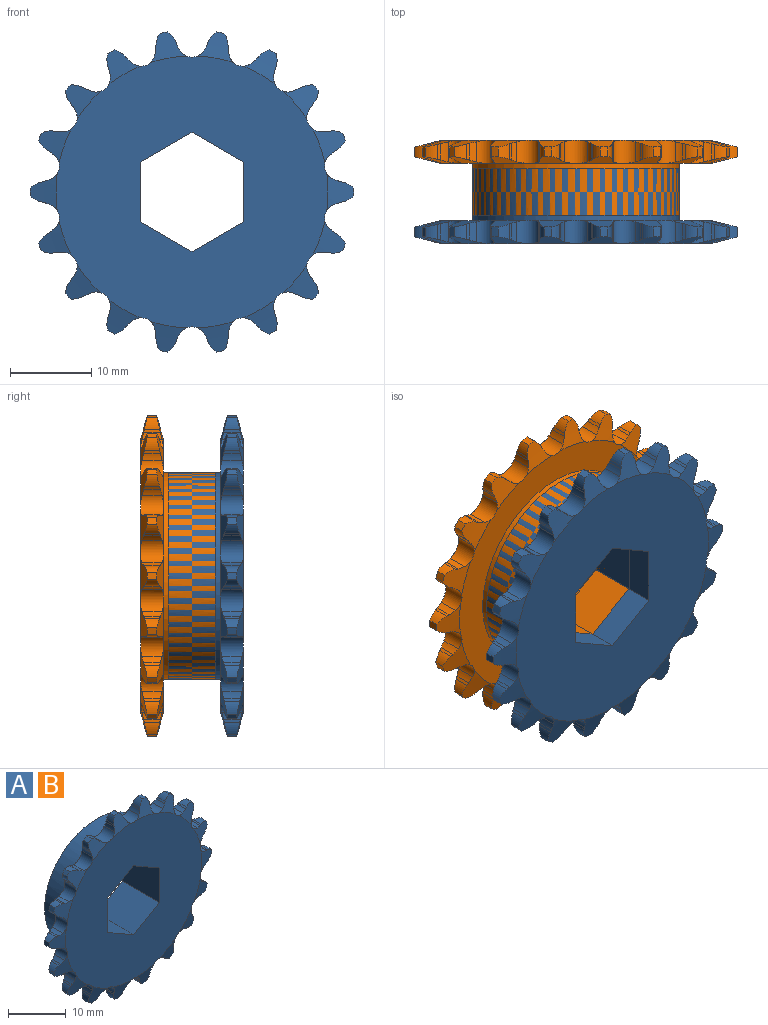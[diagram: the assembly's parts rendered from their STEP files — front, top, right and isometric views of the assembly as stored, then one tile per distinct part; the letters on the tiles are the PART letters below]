
ASSEMBLY  parts=2 mates=1
PART A: 190 faces, bbox 39.8x9.2x39.8 mm
  f0: cylinder r=12.7mm len=25.4mm, axis (0,-1,0), area 509.2mm2, adj f12,f183
  f1: cylinder r=1.74mm len=2.79mm, axis (0,1,0), area 9mm2, adj f12,f14,f16,f17,f20,f62,f170,f175
  f2: cylinder r=1.74mm len=2.79mm, axis (0,1,0), area 9mm2, adj f12,f17,f19,f20,f27,f62,f164,f169
  f3: cylinder r=1.74mm len=2.81mm, axis (0,1,0), area 9mm2, adj f11,f12,f19,f23,f27,f62,f158,f163
  f4: cylinder r=1.74mm len=2.81mm, axis (0,1,0), area 9mm2, adj f11,f12,f23,f25,f37,f62,f152,f157
  f5: cylinder r=1.74mm len=2.79mm, axis (0,1,0), area 9mm2, adj f12,f25,f28,f30,f37,f62,f146,f151
  f6: cylinder r=1.74mm len=2.79mm, axis (0,1,0), area 9mm2, adj f12,f28,f30,f31,f34,f62,f140,f145
  f7: cylinder r=2.72mm len=1.87mm, axis (0,1,0), area 2.4mm2, adj f40,f41,f42,f116
  f8: cylinder r=2.72mm len=1.87mm, axis (0,1,0), area 2.4mm2, adj f56,f57,f60,f80
  f9: cylinder r=19.91mm len=1.21mm, axis (0,1,0), area 1.1mm2, adj f10,f51,f95,f101
  f10: cone r=16.74mm half-angle=76deg, axis (0,1,0), area 8.4mm2, adj f9,f62,f95,f96,f97,f98,f99,f100
  f11: cone r=19.91mm half-angle=76deg, axis (0,-1,0), area 8.4mm2, adj f3,f4,f12,f24,f155,f156,f157,f158
  f12: plane 33.47x33.44mm, normal (0,1,0), area 370.7mm2, adj f0,f1,f2,f3,f4,f5,f6,f11
  f13: cone r=16.74mm half-angle=76deg, axis (0,1,0), area 8.4mm2, adj f61,f62,f65,f66,f67,f71,f179,f180
  f14: cone r=19.91mm half-angle=76deg, axis (0,-1,0), area 8.6mm2, adj f1,f12,f15,f173,f174,f175,f176,f177
  f15: cylinder r=19.91mm len=1.21mm, axis (0,1,0), area 1.1mm2, adj f14,f16,f173,f178
  f16: cone r=16.74mm half-angle=76deg, axis (0,1,0), area 8.6mm2, adj f1,f15,f62,f173,f174,f175,f176,f177
  f17: cone r=19.91mm half-angle=76deg, axis (0,-1,0), area 8.4mm2, adj f1,f2,f12,f18,f167,f168,f169,f170
  f18: cylinder r=19.91mm len=1.21mm, axis (0,1,0), area 1.1mm2, adj f17,f20,f167,f172
  f19: cone r=19.91mm half-angle=76deg, axis (0,-1,0), area 8.4mm2, adj f2,f3,f12,f21,f161,f162,f163,f164
  f20: cone r=16.74mm half-angle=76deg, axis (0,1,0), area 8.4mm2, adj f1,f2,f18,f62,f167,f168,f169,f170
  f21: cylinder r=19.91mm len=1.21mm, axis (0,1,0), area 1.1mm2, adj f19,f27,f161,f166
  f22: cone r=19.91mm half-angle=76deg, axis (0,-1,0), area 8.4mm2, adj f12,f61,f65,f66,f67,f71,f179,f180
  f23: cone r=16.74mm half-angle=76deg, axis (0,1,0), area 8.4mm2, adj f3,f4,f24,f62,f155,f156,f157,f158
  f24: cylinder r=19.91mm len=1.21mm, axis (0,1,0), area 1.1mm2, adj f11,f23,f155,f160
  f25: cone r=16.74mm half-angle=76deg, axis (0,1,0), area 8.4mm2, adj f4,f5,f26,f62,f149,f150,f151,f152
  f26: cylinder r=19.91mm len=1.21mm, axis (0,1,0), area 1.1mm2, adj f25,f37,f149,f154
  f27: cone r=16.74mm half-angle=76deg, axis (0,1,0), area 8.4mm2, adj f2,f3,f21,f62,f161,f162,f163,f164
  f28: cone r=19.91mm half-angle=76deg, axis (0,-1,0), area 8.4mm2, adj f5,f6,f12,f29,f143,f144,f145,f146
  f29: cylinder r=19.91mm len=1.21mm, axis (0,1,0), area 1.1mm2, adj f28,f30,f143,f148
  f30: cone r=16.74mm half-angle=76deg, axis (0,1,0), area 8.4mm2, adj f5,f6,f29,f62,f143,f144,f145,f146
  f31: cone r=19.91mm half-angle=76deg, axis (0,-1,0), area 8.6mm2, adj f6,f12,f32,f136,f137,f138,f139,f140
  f32: cylinder r=19.91mm len=1.21mm, axis (0,1,0), area 1.1mm2, adj f31,f34,f136,f142
  f33: cone r=19.91mm half-angle=76deg, axis (0,-1,0), area 8.4mm2, adj f12,f35,f129,f130,f131,f132,f133,f134
  f34: cone r=16.74mm half-angle=76deg, axis (0,1,0), area 8.6mm2, adj f6,f32,f62,f136,f137,f138,f139,f140
  f35: cylinder r=19.91mm len=1.21mm, axis (0,1,0), area 1.1mm2, adj f33,f39,f129,f135
  f36: cone r=16.74mm half-angle=76deg, axis (0,1,0), area 8.4mm2, adj f38,f62,f122,f123,f124,f125,f126,f127
  f37: cone r=19.91mm half-angle=76deg, axis (0,-1,0), area 8.4mm2, adj f4,f5,f12,f26,f149,f150,f151,f152
  f38: cylinder r=19.91mm len=1.21mm, axis (0,1,0), area 1.1mm2, adj f36,f48,f122,f128
  f39: cone r=16.74mm half-angle=76deg, axis (0,1,0), area 8.4mm2, adj f35,f62,f129,f130,f131,f132,f133,f134
  f40: cone r=19.91mm half-angle=76deg, axis (0,-1,0), area 8.5mm2, adj f7,f12,f41,f116,f117,f118,f119,f120
  f41: cylinder r=19.91mm len=1.21mm, axis (0,1,0), area 1.1mm2, adj f7,f40,f42,f121
  f42: cone r=16.74mm half-angle=76deg, axis (0,1,0), area 8.5mm2, adj f7,f41,f62,f116,f117,f118,f119,f120
  f43: cone r=19.91mm half-angle=76deg, axis (0,-1,0), area 8.4mm2, adj f12,f44,f109,f110,f111,f112,f113,f114
  f44: cylinder r=19.91mm len=1.21mm, axis (0,1,0), area 1.1mm2, adj f43,f46,f109,f115
  f45: cone r=19.91mm half-angle=76deg, axis (0,-1,0), area 8.4mm2, adj f12,f47,f102,f103,f104,f105,f106,f107
  f46: cone r=16.74mm half-angle=76deg, axis (0,1,0), area 8.4mm2, adj f44,f62,f109,f110,f111,f112,f113,f114
  f47: cylinder r=19.91mm len=1.21mm, axis (0,1,0), area 1.1mm2, adj f45,f52,f102,f108
  f48: cone r=19.91mm half-angle=76deg, axis (0,-1,0), area 8.4mm2, adj f12,f38,f122,f123,f124,f125,f126,f127
  f49: cone r=16.74mm half-angle=76deg, axis (0,1,0), area 8.4mm2, adj f50,f62,f88,f89,f90,f91,f92,f93
  f50: cylinder r=19.91mm len=1.21mm, axis (0,1,0), area 1.1mm2, adj f49,f63,f88,f94
  f51: cone r=19.91mm half-angle=76deg, axis (0,-1,0), area 8.4mm2, adj f9,f12,f95,f96,f97,f98,f99,f100
  f52: cone r=16.74mm half-angle=76deg, axis (0,1,0), area 8.4mm2, adj f47,f62,f102,f103,f104,f105,f106,f107
  f53: cylinder r=19.91mm len=1.21mm, axis (0,1,0), area 1.1mm2, adj f54,f55,f81,f87
  f54: cone r=19.91mm half-angle=76deg, axis (0,-1,0), area 8.4mm2, adj f12,f53,f81,f82,f83,f84,f85,f86
  f55: cone r=16.74mm half-angle=76deg, axis (0,1,0), area 8.4mm2, adj f53,f62,f81,f82,f83,f84,f85,f86
  f56: cylinder r=19.91mm len=1.21mm, axis (0,1,0), area 1.1mm2, adj f8,f57,f60,f75
  f57: cone r=19.91mm half-angle=76deg, axis (0,-1,0), area 8.5mm2, adj f8,f12,f56,f75,f76,f77,f78,f79
  f58: cylinder r=19.91mm len=1.21mm, axis (0,1,0), area 1.1mm2, adj f59,f64,f68,f74
  f59: cone r=19.91mm half-angle=76deg, axis (0,-1,0), area 8.4mm2, adj f12,f58,f68,f69,f70,f71,f72,f73
  f60: cone r=16.74mm half-angle=76deg, axis (0,1,0), area 8.5mm2, adj f8,f56,f62,f75,f76,f77,f78,f79
  f61: cylinder r=19.91mm len=1.21mm, axis (0,1,0), area 1.1mm2, adj f13,f22,f67,f179
  f62: plane 33.47x33.44mm, normal (0,-1,0), area 737.2mm2, adj f1,f2,f3,f4,f5,f6,f10,f13
  f63: cone r=19.91mm half-angle=76deg, axis (0,-1,0), area 8.4mm2, adj f12,f50,f88,f89,f90,f91,f92,f93
  f64: cone r=16.74mm half-angle=76deg, axis (0,1,0), area 8.4mm2, adj f58,f62,f68,f69,f70,f71,f72,f73
  f65: cylinder r=4.28mm len=2.47mm, axis (0,1,0), area 2.1mm2, adj f13,f22,f66,f71
  f66: plane 2.05x0.35mm, normal (-0.92,0,0.38), area 0.7mm2, adj f13,f22,f65,f67
  f67: cylinder r=2.72mm len=1.87mm, axis (0,1,0), area 2.4mm2, adj f13,f22,f61,f66
  f68: cylinder r=2.72mm len=1.87mm, axis (0,1,0), area 2.4mm2, adj f58,f59,f64,f69
  f69: plane 2.05x0.35mm, normal (0.92,0,0.38), area 0.7mm2, adj f59,f64,f68,f70
  f70: cylinder r=4.28mm len=2.47mm, axis (0,1,0), area 2.1mm2, adj f59,f64,f69,f71
  f71: cylinder r=1.74mm len=2.85mm, axis (0,1,0), area 9mm2, adj f12,f13,f22,f59,f62,f64,f65,f70
  f72: cylinder r=4.28mm len=2.47mm, axis (0,1,0), area 2.1mm2, adj f59,f64,f73,f78
  f73: plane 2.05x0.38mm, normal (-1,0,0.04), area 0.7mm2, adj f59,f64,f72,f74
  f74: cylinder r=2.72mm len=1.87mm, axis (0,1,0), area 2.4mm2, adj f58,f59,f64,f73
  f75: cylinder r=2.72mm len=1.87mm, axis (0,1,0), area 2.4mm2, adj f56,f57,f60,f76
  f76: plane 2.05x0.28mm, normal (0.74,0,0.68), area 0.7mm2, adj f57,f60,f75,f77
  f77: cylinder r=4.28mm len=2.47mm, axis (0,1,0), area 2.1mm2, adj f57,f60,f76,f78
  f78: cylinder r=1.74mm len=2.79mm, axis (0,1,0), area 9mm2, adj f12,f57,f59,f60,f62,f64,f72,f77
  f79: cylinder r=4.28mm len=2.47mm, axis (0,1,0), area 2.1mm2, adj f57,f60,f80,f84
  f80: plane 2.05x0.36mm, normal (-0.95,0,-0.3), area 0.7mm2, adj f8,f57,f60,f79
  f81: cylinder r=2.72mm len=1.87mm, axis (0,1,0), area 2.4mm2, adj f53,f54,f55,f82
  f82: plane 2.05x0.34mm, normal (0.46,0,0.89), area 0.7mm2, adj f54,f55,f81,f83
  f83: cylinder r=4.28mm len=2.47mm, axis (0,1,0), area 2.1mm2, adj f54,f55,f82,f84
  f84: cylinder r=1.74mm len=2.79mm, axis (0,1,0), area 9mm2, adj f12,f54,f55,f57,f60,f62,f79,f83
  f85: cylinder r=4.28mm len=2.47mm, axis (0,1,0), area 2.1mm2, adj f54,f55,f86,f91
  f86: plane 2.05x0.3mm, normal (-0.79,0,-0.61), area 0.7mm2, adj f54,f55,f85,f87
  f87: cylinder r=2.72mm len=1.87mm, axis (0,1,0), area 2.4mm2, adj f53,f54,f55,f86
  f88: cylinder r=2.72mm len=1.87mm, axis (0,1,0), area 2.4mm2, adj f49,f50,f63,f89
  f89: plane 2.05x0.38mm, normal (0.13,0,0.99), area 0.7mm2, adj f49,f63,f88,f90
  f90: cylinder r=4.28mm len=2.47mm, axis (0,1,0), area 2.1mm2, adj f49,f63,f89,f91
  f91: cylinder r=1.74mm len=2.79mm, axis (0,1,0), area 9mm2, adj f12,f49,f54,f55,f62,f63,f85,f90
  f92: cylinder r=4.28mm len=2.47mm, axis (0,1,0), area 2.1mm2, adj f49,f63,f93,f98
  f93: plane 2.05x0.32mm, normal (-0.54,0,-0.84), area 0.7mm2, adj f49,f63,f92,f94
  f94: cylinder r=2.72mm len=1.87mm, axis (0,1,0), area 2.4mm2, adj f49,f50,f63,f93
  f95: cylinder r=2.72mm len=1.87mm, axis (0,1,0), area 2.4mm2, adj f9,f10,f51,f96
  f96: plane 2.05x0.37mm, normal (-0.22,0,0.98), area 0.7mm2, adj f10,f51,f95,f97
  f97: cylinder r=4.28mm len=2.47mm, axis (0,1,0), area 2.1mm2, adj f10,f51,f96,f98
  f98: cylinder r=1.74mm len=2.81mm, axis (0,1,0), area 9mm2, adj f10,f12,f49,f51,f62,f63,f92,f97
  f99: cylinder r=4.28mm len=2.47mm, axis (0,1,0), area 2.1mm2, adj f10,f51,f100,f105
  f100: plane 2.05x0.37mm, normal (-0.22,0,-0.98), area 0.7mm2, adj f10,f51,f99,f101
  f101: cylinder r=2.72mm len=1.87mm, axis (0,1,0), area 2.4mm2, adj f9,f10,f51,f100
  f102: cylinder r=2.72mm len=1.87mm, axis (0,1,0), area 2.4mm2, adj f45,f47,f52,f103
  f103: plane 2.05x0.32mm, normal (-0.54,0,0.84), area 0.7mm2, adj f45,f52,f102,f104
  f104: cylinder r=4.28mm len=2.47mm, axis (0,1,0), area 2.1mm2, adj f45,f52,f103,f105
  f105: cylinder r=1.74mm len=2.81mm, axis (0,1,0), area 9mm2, adj f10,f12,f45,f51,f52,f62,f99,f104
  f106: cylinder r=4.28mm len=2.47mm, axis (0,1,0), area 2.1mm2, adj f45,f52,f107,f112
  f107: plane 2.05x0.38mm, normal (0.13,0,-0.99), area 0.7mm2, adj f45,f52,f106,f108
  f108: cylinder r=2.72mm len=1.87mm, axis (0,1,0), area 2.4mm2, adj f45,f47,f52,f107
  f109: cylinder r=2.72mm len=1.87mm, axis (0,1,0), area 2.4mm2, adj f43,f44,f46,f110
  f110: plane 2.05x0.3mm, normal (-0.79,0,0.61), area 0.7mm2, adj f43,f46,f109,f111
  f111: cylinder r=4.28mm len=2.47mm, axis (0,1,0), area 2.1mm2, adj f43,f46,f110,f112
  f112: cylinder r=1.74mm len=2.79mm, axis (0,1,0), area 9mm2, adj f12,f43,f45,f46,f52,f62,f106,f111
  f113: cylinder r=4.28mm len=2.47mm, axis (0,1,0), area 2.1mm2, adj f43,f46,f114,f118
  f114: plane 2.05x0.34mm, normal (0.46,0,-0.89), area 0.7mm2, adj f43,f46,f113,f115
  f115: cylinder r=2.72mm len=1.87mm, axis (0,1,0), area 2.4mm2, adj f43,f44,f46,f114
  f116: plane 2.05x0.36mm, normal (-0.95,0,0.3), area 0.7mm2, adj f7,f40,f42,f117
  f117: cylinder r=4.28mm len=2.47mm, axis (0,1,0), area 2.1mm2, adj f40,f42,f116,f118
  f118: cylinder r=1.74mm len=2.79mm, axis (0,1,0), area 9mm2, adj f12,f40,f42,f43,f46,f62,f113,f117
  f119: cylinder r=4.28mm len=2.47mm, axis (0,1,0), area 2.1mm2, adj f40,f42,f120,f125
  f120: plane 2.05x0.28mm, normal (0.74,0,-0.68), area 0.7mm2, adj f40,f42,f119,f121
  f121: cylinder r=2.72mm len=1.87mm, axis (0,1,0), area 2.4mm2, adj f40,f41,f42,f120
  f122: cylinder r=2.72mm len=1.87mm, axis (0,1,0), area 2.4mm2, adj f36,f38,f48,f123
  f123: plane 2.05x0.38mm, normal (-1,0,-0.04), area 0.7mm2, adj f36,f48,f122,f124
  f124: cylinder r=4.28mm len=2.47mm, axis (0,1,0), area 2.1mm2, adj f36,f48,f123,f125
  f125: cylinder r=1.74mm len=2.79mm, axis (0,1,0), area 9mm2, adj f12,f36,f40,f42,f48,f62,f119,f124
  f126: cylinder r=4.28mm len=2.47mm, axis (0,1,0), area 2.1mm2, adj f36,f48,f127,f132
  f127: plane 2.05x0.35mm, normal (0.92,0,-0.38), area 0.7mm2, adj f36,f48,f126,f128
  f128: cylinder r=2.72mm len=1.87mm, axis (0,1,0), area 2.4mm2, adj f36,f38,f48,f127
  f129: cylinder r=2.72mm len=1.87mm, axis (0,1,0), area 2.4mm2, adj f33,f35,f39,f130
  f130: plane 2.05x0.35mm, normal (-0.92,0,-0.38), area 0.7mm2, adj f33,f39,f129,f131
  f131: cylinder r=4.28mm len=2.47mm, axis (0,1,0), area 2.1mm2, adj f33,f39,f130,f132
  f132: cylinder r=1.74mm len=2.85mm, axis (0,1,0), area 9mm2, adj f12,f33,f36,f39,f48,f62,f126,f131
  f133: cylinder r=4.28mm len=2.47mm, axis (0,1,0), area 2.1mm2, adj f33,f39,f134,f139
  f134: plane 2.05x0.38mm, normal (1,0,-0.04), area 0.7mm2, adj f33,f39,f133,f135
  f135: cylinder r=2.72mm len=1.87mm, axis (0,1,0), area 2.4mm2, adj f33,f35,f39,f134
  f136: cylinder r=2.72mm len=1.87mm, axis (0,1,0), area 2.4mm2, adj f31,f32,f34,f137
  f137: plane 2.05x0.28mm, normal (-0.74,0,-0.68), area 0.7mm2, adj f31,f34,f136,f138
  f138: cylinder r=4.28mm len=2.47mm, axis (0,1,0), area 2.1mm2, adj f31,f34,f137,f139
  f139: cylinder r=1.74mm len=2.79mm, axis (0,1,0), area 9mm2, adj f12,f31,f33,f34,f39,f62,f133,f138
  f140: cylinder r=4.28mm len=2.47mm, axis (0,1,0), area 2.1mm2, adj f6,f31,f34,f141
  f141: plane 2.05x0.36mm, normal (0.95,0,0.3), area 0.7mm2, adj f31,f34,f140,f142
  f142: cylinder r=2.72mm len=1.87mm, axis (0,1,0), area 2.4mm2, adj f31,f32,f34,f141
  f143: cylinder r=2.72mm len=1.87mm, axis (0,1,0), area 2.4mm2, adj f28,f29,f30,f144
  f144: plane 2.05x0.34mm, normal (-0.46,0,-0.89), area 0.7mm2, adj f28,f30,f143,f145
  f145: cylinder r=4.28mm len=2.47mm, axis (0,1,0), area 2.1mm2, adj f6,f28,f30,f144
  f146: cylinder r=4.28mm len=2.47mm, axis (0,1,0), area 2.1mm2, adj f5,f28,f30,f147
  f147: plane 2.05x0.3mm, normal (0.79,0,0.61), area 0.7mm2, adj f28,f30,f146,f148
  f148: cylinder r=2.72mm len=1.87mm, axis (0,1,0), area 2.4mm2, adj f28,f29,f30,f147
  f149: cylinder r=2.72mm len=1.87mm, axis (0,1,0), area 2.4mm2, adj f25,f26,f37,f150
  f150: plane 2.05x0.38mm, normal (-0.13,0,-0.99), area 0.7mm2, adj f25,f37,f149,f151
  f151: cylinder r=4.28mm len=2.47mm, axis (0,1,0), area 2.1mm2, adj f5,f25,f37,f150
  f152: cylinder r=4.28mm len=2.47mm, axis (0,1,0), area 2.1mm2, adj f4,f25,f37,f153
  f153: plane 2.05x0.32mm, normal (0.54,0,0.84), area 0.7mm2, adj f25,f37,f152,f154
  f154: cylinder r=2.72mm len=1.87mm, axis (0,1,0), area 2.4mm2, adj f25,f26,f37,f153
  f155: cylinder r=2.72mm len=1.87mm, axis (0,1,0), area 2.4mm2, adj f11,f23,f24,f156
  f156: plane 2.05x0.37mm, normal (0.22,0,-0.98), area 0.7mm2, adj f11,f23,f155,f157
  f157: cylinder r=4.28mm len=2.47mm, axis (0,1,0), area 2.1mm2, adj f4,f11,f23,f156
  f158: cylinder r=4.28mm len=2.47mm, axis (0,1,0), area 2.1mm2, adj f3,f11,f23,f159
  f159: plane 2.05x0.37mm, normal (0.22,0,0.98), area 0.7mm2, adj f11,f23,f158,f160
  f160: cylinder r=2.72mm len=1.87mm, axis (0,1,0), area 2.4mm2, adj f11,f23,f24,f159
  f161: cylinder r=2.72mm len=1.87mm, axis (0,1,0), area 2.4mm2, adj f19,f21,f27,f162
  f162: plane 2.05x0.32mm, normal (0.54,0,-0.84), area 0.7mm2, adj f19,f27,f161,f163
  f163: cylinder r=4.28mm len=2.47mm, axis (0,1,0), area 2.1mm2, adj f3,f19,f27,f162
  f164: cylinder r=4.28mm len=2.47mm, axis (0,1,0), area 2.1mm2, adj f2,f19,f27,f165
  f165: plane 2.05x0.38mm, normal (-0.13,0,0.99), area 0.7mm2, adj f19,f27,f164,f166
  f166: cylinder r=2.72mm len=1.87mm, axis (0,1,0), area 2.4mm2, adj f19,f21,f27,f165
  f167: cylinder r=2.72mm len=1.87mm, axis (0,1,0), area 2.4mm2, adj f17,f18,f20,f168
  f168: plane 2.05x0.3mm, normal (0.79,0,-0.61), area 0.7mm2, adj f17,f20,f167,f169
  f169: cylinder r=4.28mm len=2.47mm, axis (0,1,0), area 2.1mm2, adj f2,f17,f20,f168
  f170: cylinder r=4.28mm len=2.47mm, axis (0,1,0), area 2.1mm2, adj f1,f17,f20,f171
  f171: plane 2.05x0.34mm, normal (-0.46,0,0.89), area 0.7mm2, adj f17,f20,f170,f172
  f172: cylinder r=2.72mm len=1.87mm, axis (0,1,0), area 2.4mm2, adj f17,f18,f20,f171
  f173: cylinder r=2.72mm len=1.87mm, axis (0,1,0), area 2.4mm2, adj f14,f15,f16,f174
  f174: plane 2.05x0.36mm, normal (0.95,0,-0.3), area 0.7mm2, adj f14,f16,f173,f175
  f175: cylinder r=4.28mm len=2.47mm, axis (0,1,0), area 2.1mm2, adj f1,f14,f16,f174
  f176: cylinder r=4.28mm len=2.47mm, axis (0,1,0), area 2.1mm2, adj f14,f16,f177,f182
  f177: plane 2.05x0.28mm, normal (-0.74,0,0.68), area 0.7mm2, adj f14,f16,f176,f178
  f178: cylinder r=2.72mm len=1.87mm, axis (0,1,0), area 2.4mm2, adj f14,f15,f16,f177
  f179: cylinder r=2.72mm len=1.87mm, axis (0,1,0), area 2.4mm2, adj f13,f22,f61,f180
  f180: plane 2.05x0.38mm, normal (1,0,0.04), area 0.7mm2, adj f13,f22,f179,f181
  f181: cylinder r=4.28mm len=2.47mm, axis (0,1,0), area 2.1mm2, adj f13,f22,f180,f182
  f182: cylinder r=1.74mm len=2.79mm, axis (0,1,0), area 9mm2, adj f12,f13,f14,f16,f22,f62,f176,f181
  f183: plane 25.4x25.4mm, normal (0,1,0), area 366.5mm2, adj f0,f184,f185,f186,f187,f188,f189
  f184: plane 9.18x6.36mm, normal (0.5,0,-0.87), area 67.4mm2, adj f62,f183,f185,f189
  f185: plane 9.18x6.36mm, normal (-0.5,0,-0.87), area 67.4mm2, adj f62,f183,f184,f186
  f186: plane 9.18x7.35mm, normal (-1,0,0), area 67.4mm2, adj f62,f183,f185,f187
  f187: plane 9.18x6.36mm, normal (-0.5,0,0.87), area 67.4mm2, adj f62,f183,f186,f188
  f188: plane 9.18x6.36mm, normal (0.5,0,0.87), area 67.4mm2, adj f62,f183,f187,f189
  f189: plane 9.18x7.35mm, normal (1,0,0), area 67.4mm2, adj f62,f183,f184,f188
PART B: same geometry as A
PLACE A t=(-15.41,-7.56,4.69)mm
PLACE B rot(axis=(1,0,0),180deg) t=(-15.41,-0.52,4.69)mm
MATE revolute B.f0 <-> A.f0  axis (0,-1,0) through (-15.41,-6.9,4.69)mm
